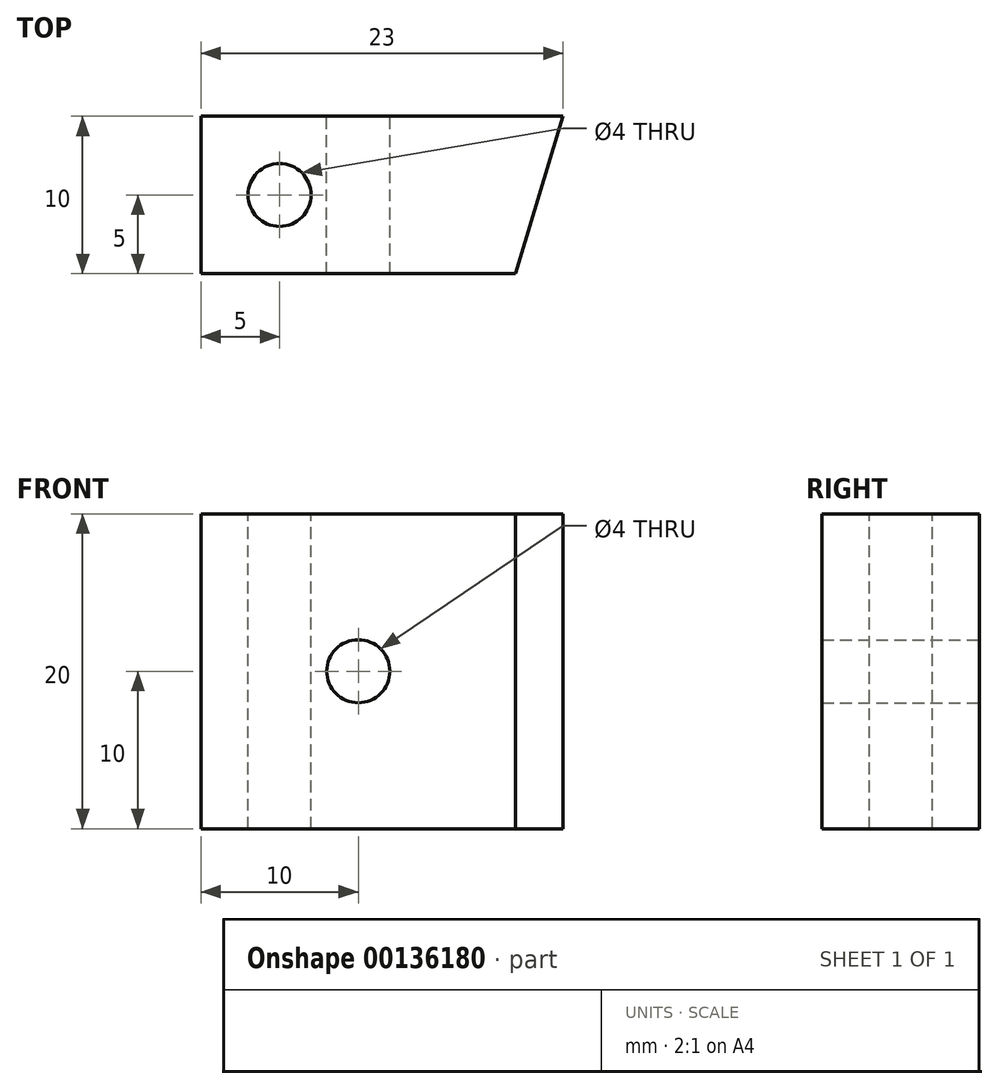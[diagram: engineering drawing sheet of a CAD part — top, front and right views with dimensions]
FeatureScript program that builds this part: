
annotation { "Feature Type Name" : "Feature", "Feature Type Description" : "" }
export const myFeature = defineFeature(function(context is Context, id is Id, definition is map)
    precondition{}
    {
        {
            var Q0;
            Q0=qCreatedBy(makeId("Top.planeOp"),FACE);
            var sketch = newSketch(context, id + "F0", { "sketchPlane" : qUnion([Q0])});
            skLineSegment(sketch, "E0", {"start": v(0, 0) * mm, "end": v(0, 10) * mm});
            skLineSegment(sketch, "E1", {"start": v(0, 10) * mm, "end": v(20, 10) * mm});
            skLineSegment(sketch, "E2", {"start": v(20, 10) * mm, "end": v(20, 0) * mm});
            skLineSegment(sketch, "E3", {"start": v(20, 0) * mm, "end": v(0, 0) * mm});
            skLineSegment(sketch, "E4", {"start": v(20, 10) * mm, "end": v(23, 10) * mm});
            skLineSegment(sketch, "E5", {"start": v(23, 10) * mm, "end": v(20, 0) * mm});
            skSolve(sketch);
        }
        {
            var Q0;
            Q0=makeQuery(id+"F0.imprint","IMPRINT",FACE,{"disambiguationData":[TD([[makeQuery(id+"F0.imprint","IMPRINT",EDGE,{"derivedFrom":sQuery(id+"F0.wireOp",EDGE,"E0")}),-1.0]])]});
            extrude(context, id + "F1", {"entities" : qUnion([Q0]), "depth" : 10 * mm});
        }
        {
            var Q0;
            Q0 = qSketchRegion(id + "F0", true);
            extrude(context, id + "F2", {"entities" : qUnion([Q0]), "operationType" : NewBodyOperationType.ADD, "depth" : 10 * mm});
        }
        {
            var Q0;
            Q0 = qSketchRegion(id + "F0", true);
            extrude(context, id + "F3", {"entities" : qUnion([Q0]), "operationType" : NewBodyOperationType.ADD, "depth" : 20 * mm});
        }
        {
            var Q0;
            {var subQ0=sQuery(id+"F0.wireOp",EDGE,"E4");var subQ1=sQuery(id+"F0.wireOp",EDGE,"E1");Q0=makeQuery(id+"F3.boolean.opBoolean","MERGE",FACE,{"derivedFrom":[makeQuery(id+"F2.boolean.opBoolean","MERGE",FACE,{"derivedFrom":[makeQuery(id+"F1.opExtrude","SWEPT_FACE",FACE,{"disambiguationData":[OSD([subQ1])]}),makeQuery(id+"F2.opExtrude","SWEPT_FACE",FACE,{"disambiguationData":[OSD([subQ1,subQ0])]})]}),makeQuery(id+"F3.opExtrude","SWEPT_FACE",FACE,{"disambiguationData":[OSD([subQ1,subQ0])]})]});}
            var sketch = newSketch(context, id + "F4", { "sketchPlane" : qUnion([Q0])});
            skCircle(sketch, "E6", {"center": v(-10, 10) * mm, "radius": 2 * mm});
            skSolve(sketch);
        }
        {
            var Q0;
            Q0=makeQuery(id+"F4.imprint","IMPRINT",FACE,{"disambiguationData":[TD([[makeQuery(id+"F4.imprint","IMPRINT",EDGE,{"derivedFrom":sQuery(id+"F4.wireOp",EDGE,"E6")}),1.0]])]});
            extrude(context, id + "F5", {"entities" : qUnion([Q0]), "operationType" : NewBodyOperationType.REMOVE, "oppositeDirection" : true, "depth" : 25 * mm});
        }
        {
            var Q0;
            Q0=makeQuery(id+"F3.opExtrude","CAP_FACE",FACE,{"disambiguationData":[OSD([sQuery(id+"F0.wireOp",EDGE,"E0"),sQuery(id+"F0.wireOp",EDGE,"E1"),sQuery(id+"F0.wireOp",EDGE,"E3"),sQuery(id+"F0.wireOp",EDGE,"E4"),sQuery(id+"F0.wireOp",EDGE,"E5")])],"isStart":false});
            var sketch = newSketch(context, id + "F6", { "sketchPlane" : qUnion([Q0])});
            skCircle(sketch, "E7", {"center": v(5, 5) * mm, "radius": 2 * mm});
            skSolve(sketch);
        }
        {
            var Q0;
            Q0=makeQuery(id+"F6.imprint","IMPRINT",FACE,{"disambiguationData":[TD([[makeQuery(id+"F6.imprint","IMPRINT",EDGE,{"derivedFrom":sQuery(id+"F6.wireOp",EDGE,"E7")}),1.0]])]});
            extrude(context, id + "F7", {"entities" : qUnion([Q0]), "operationType" : NewBodyOperationType.REMOVE, "oppositeDirection" : true, "depth" : 25 * mm});
        }
    });
